# Revit family: AI13-P4W9S1BBZ5
name_source: partatom
category: Luminarias
revit_build: Autodesk Revit 2017 (Build: 20160225_1515(x64)
units: mm (PartAtom-declared; Revit-internal decimal feet)

## family parameters
Compartido = Sí
Corte con vacíos al cargar = No
Cota de conector redondo = Diámetro de uso
Número OmniClass = 23.80.70.00
Origen de luz = No
Punto de cálculo de habitación = No
Se basa en plano de trabajo = No
Siempre vertical = Sí
Tipo de pieza = Normal
Título OmniClass = Lighting

## types (1)
- AI13-P4W9S1BBZ5
    Acabado = Gris urbà, Transparent
    CRI = 90
    Catálogo = Outdoor
    CodigoGubimclass = 50.60.50.20
    CodigoOmniclass = 21-04 50 40
    CodigoUniclass2015 = EF_70_80
    CodigoUniformat2010 = D5040
    DescripcionGubimclass = Iluminación interior
    DescripcionOmniclass = Lighting
    DescripcionUniclass2015 = Lighting
    DescripcionUniformat2010 = Lighting
    EAN13 = 8435575373884
    Eficiencia energética = LED A++
    Etiqueta V/f = 12V/Max. 350mA
    Fabricante = LEDS C4
    Familia = Max ø58mm Trimless
    FechaVersion = Creada: 03/06/2021
    Ficha = https://files.leds-c4.com
    Fotometría = https://files.leds-c4.com
    IK = IK10
    IMC = https://files.leds-c4.com
    IP = IP66
    IfcExportAs = IfcLightFixture
    IfcExportType = NOTDEFINED
    Imagen web = https://files.leds-c4.com
    LDT = https://files.leds-c4.com
    Lumenes reales (lm) = 286
    Material = Alumini, Vidre
    Peso neto (KG) = 0.37
    Producto descatalogado = Catalogado
    Rayo de luz = NARROW
    Referencia = AI13-P4W9S1BBZ5
    Temperatura color led (K) = Blanc càlid - 3000K
    Tender text (Castellano) = LEDS C4
Max ø58mm Trimless
AI13-P4W9S1BBZ5

Empotrable de suelo d’ús exterior per il·luminar cap amunt. 
Metres del cable inclòs: 1. Material de l'estructura: Alumini. Acabat estructura: Gris urbà. Material del difusor: Vidre. Acabat difusor: Transparent. Protecció contra els raigs ultraviolats. Garantia: 5 Anys.

Pes net del producte (Kg): 0.37
Amplada o diàmetre del producte (mm): 58
Alçada del producte (mm): 90

Classe 3. Prova fil incandescent: 850. IP: IP66. IK: IK10. LED. Nº de portalàmpades o Leds: 1. Marca del LED: CREE. Potència màxima de la font de llum: 4W. Temperatura de color: 3000K. Índex de reproducció cromàtica: 90. Steps Mac Adam: 3. Diàmetre màxim de la bombeta que admet la lluminària: 50.000h L80B20. UGR: 9.9. Risc fotobiològic: RG2. Flux real (lm): 286. Lm / W reals: 72. Voltatge: 12. Equip inclòs: No, pero el necessita. Potència total: 4.
    Tender text (English) = LEDS C4
Max ø58mm Trimless
AI13-P4W9S1BBZ5

Recessed uplighting for outdoor use. 

For uplighting. Metres of cable included: 1. Structure material: Aluminium. Structure finish: Urban grey. Diffuser material: Glass. Diffuser finish: Transparent. UV protection. Warranty: 5 Years.

Product net weight (Kg): 0.37
Product width or diameter (mm): 58
Product height (mm): 90

Class 3. Glow wire test: 850. IP: IP66. IK: IK10. LED. No. of lampholders or LEDs: 1. LED brand: CREE. Maximum power of light source: 4W. Colour temperature: 3000K. Colour rendering index: 90. MacAdam Steps: 3. Maximum diameter of luminaire bulb: 50.000h L80B20. UGR: 9.9. Photobiological risk: RG2. Real flux (lm): 286. Real lm/W: 72. Voltage: 12. Equipment included: No, but it is needed. Total power: 4.
    Tipo = Empotrable de suelo
    Vatios (W) = 4
    Versión = v1
